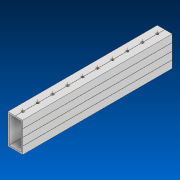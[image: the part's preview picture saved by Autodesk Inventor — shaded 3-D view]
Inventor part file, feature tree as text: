
AUTODESK INVENTOR PART (.ipt)
format: ipt  version: 2022.2 (Build 262287000, 287)  size: 446,976 bytes
history: native  units: in
note: dims shown in document units (in); Inventor stores cm internally (conversion verified against a paired STEP export)
features: other x11, extrude x1, pattern_linear x1, sketch x1
ambient origin geometry x8: Origin, YZ Plane, XZ Plane, XY Plane, X Axis, Y Axis, Z Axis, Center Point
bodies: Solid1 (feature_tree)
feature tree (14):
  extrude  "Extrusion1"  Depth=2.0in
  other  "Work Axis1"
  pattern_linear  "Rectangular Pattern1"  Spacing1=49.0in  [1 undecoded]
  sketch  "Sketch1"  dims[d0=1.0in d1=2.0in d2=49.0in d3=0.0in d4=3.937in d6=1.0in]
  other  "Work Axis2"
  other  "Work Axis3"
  other  "Work Axis4"
  other  "Work Axis5"
  other  "Work Axis6"
  other  "Work Axis7"
  other  "Work Axis8"
  other  "Work Axis9"
  other  "Work Axis10"
  other  "Cut-Extrude2"
note: 1 required parameter value undecoded (feature->parameter linkage not recoverable at this tier; creation-order binding heuristic only, values carry confidence <= 0.55)
